FCSTD DOCUMENT  (FreeCAD 0.18R16161 (Git))
Label:  FFFFFFF
License: All rights reserved
LicenseURL: http://en.wikipedia.org/wiki/All_rights_reserved
objects: Sketcher::SketchObject×1, PartDesign::Body×1
note: 2 computed .brp shape members not serialized (recipe doc carries the construction recipe); baked Part::Feature solids carry a one-line shape summary decoded from their .brp

FEATURE [Sketcher::SketchObject] Sketch
  MapMode = 5
  Placement = pos=(0,0,0) rot=(1,0,0;1.5708rad)
  Support = -> [XZ_Plane]
  sketch-geometry (11):
    g0: GeomPoint X=40.0344 Y=36.544 Z=0
    g1: LineSegment StartX=76.0344 StartY=36.544 StartZ=0 EndX=76.0344 EndY=-3.45601 EndZ=0
    g2: LineSegment StartX=40.0344 StartY=36.544 StartZ=0 EndX=40.0344 EndY=-3.45601 EndZ=0
    g3: LineSegment StartX=76.0344 StartY=36.544 StartZ=0 EndX=40.0344 EndY=36.544 EndZ=0
    g4: LineSegment StartX=96.0344 StartY=-3.45601 StartZ=0 EndX=76.0344 EndY=-3.45601 EndZ=0
    g5: LineSegment StartX=76.0344 StartY=-3.45601 StartZ=0 EndX=40.0344 EndY=-3.45601 EndZ=0
    g6: LineSegment StartX=40.0344 StartY=-3.45601 StartZ=0 EndX=20.0344 EndY=-3.45601 EndZ=0
    g7: LineSegment StartX=96.0344 StartY=-3.45601 StartZ=0 EndX=96.0344 EndY=36.544 EndZ=0
    g8: LineSegment StartX=76.0344 StartY=36.544 StartZ=0 EndX=96.0344 EndY=36.544 EndZ=0
    g9: LineSegment StartX=40.0344 StartY=36.544 StartZ=0 EndX=20.0344 EndY=36.544 EndZ=0
    g10: LineSegment StartX=20.0344 StartY=36.544 StartZ=0 EndX=20.0344 EndY=-3.45601 EndZ=0
  constraints (28):
    c: DistanceX(g0,g3) = 36
    c: Coincident(g2,g0)
    c: Vertical(g2)
    c: Coincident(g3,g0)
    c: Horizontal(g3)
    c: DistanceX(g6,g2) = 20
    c: Coincident(g4,g1)
    c: Horizontal(g4)
    c: Coincident(g5,g1)
    c: Coincident(g5,g2)
    c: Horizontal(g5)
    c: Coincident(g6,g2)
    c: Horizontal(g6)
    c: Coincident(g7,g4)
    c: Perpendicular(g7,g4)
    c: DistanceX(g2,g1) = 36
    c: DistanceX(g4,g4) = 20
    c: DistanceY(g7,g7) = 40
    c: DistanceY(g1,g1) = 40
    c: DistanceY(g2,g2) = 40
    c: Coincident(g8,g1)
    c: Coincident(g8,g7)
    c: DistanceX(g8,g8) = 20
    c: Coincident(g9,g0)
    c: DistanceX(g9,g9) = 20
    c: Coincident(g10,g9)
    c: Coincident(g10,g6)
    c: DistanceY(g10,g10) = 40
FEATURE [PartDesign::Body] Body
  Group = -> [Sketch]
  Origin = -> Origin
